# Revit family: 101010010221804
name_source: partatom
category: Generic Models
revit_build: Autodesk Revit 2018 (Build: 20190510_1515(x64)
units: mm (PartAtom-declared; Revit-internal decimal feet)

## family parameters
Always vertical = No
Can host rebar = No
Cut with Voids When Loaded = No
Part Type = Normal
Room Calculation Point = No
Round Connector Dimension = Use Diameter
Shared = No
Work Plane-Based = No

## types (1)
- SEPARADOR MOLDAJE RUEDA 25MM BOLSA 500UN
    Aplicacion = Se insertan a modo de clip a presión en forma vertical, en elacero de refuerzo estructural (barras), más cercanas al encofrado ó fenólica. (4 Un. x m2 Aprox.)
    Color = Negro
    Description = Se usa para distanciar una barra o malla, del encofrado o fenólico.
    Dimension = 25 mm  [stored 0.082021 ft]
    Empresa = CNP SPA.
    Espesor = 0 mm  [stored 0 ft]
    Material = PEAD
    Model = SEPARADOR MOLDAJE RUEDA
    Nombre SKU = SEPARADOR MOLDAJE RUEDA 25MM BOLSA 500UN
    Num SKUs = 101010010221804
    URL = https://www.empresascnp.cl
    Unidad = Bolsa 500 Un.
    Url Ficha tecnica = https://empresascnp.cl
    Uso = Para distanciar una barra o malla, del encofrado, y placa de fenólico en muros, en trabajos verticales, y vigas de losa.
    Ventajas = Mantiene un mínimo contacto con el moldaje. Evitan que las barras se curven, desplacen ó se muevan durante el vaciado del hormigón.

note: [stored X ft] marks values corroborated as IEEE doubles in the binary element streams (Revit-internal decimal feet)

## geometry (parser evidence)
native form markers: Sweep x2
no freeform markers — native parametric forms only
